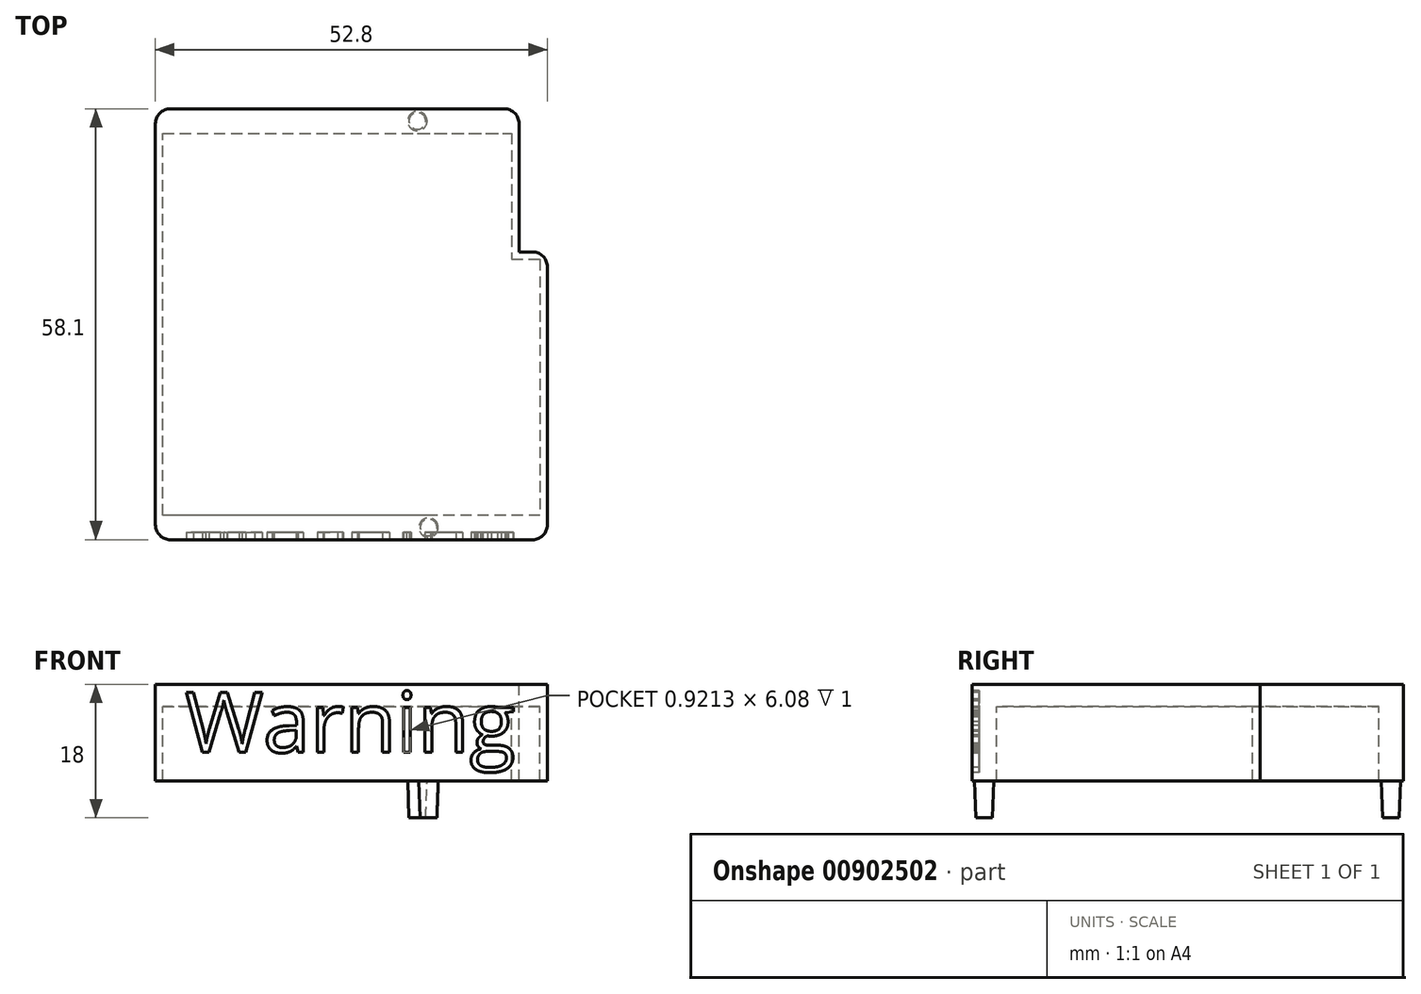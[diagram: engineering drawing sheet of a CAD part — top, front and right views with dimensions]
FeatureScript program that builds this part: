
annotation { "Feature Type Name" : "Feature", "Feature Type Description" : "" }
export const myFeature = defineFeature(function(context is Context, id is Id, definition is map)
    precondition{}
    {
        {
            var Q0;
            Q0=qCreatedBy(makeId("Top.planeOp"),FACE);
            var sketch = newSketch(context, id + "F0", { "sketchPlane" : qUnion([Q0])});
            skLineSegment(sketch, "E0", {"start": v(0, 0) * mm, "end": v(-50.8, 0) * mm});
            skLineSegment(sketch, "E1", {"start": v(-50.8, 0) * mm, "end": v(-50.8, 51.5) * mm});
            skLineSegment(sketch, "E2", {"start": v(-50.8, 51.5) * mm, "end": v(-3.81, 51.5) * mm});
            skLineSegment(sketch, "E3", {"start": v(-3.81, 51.5) * mm, "end": v(-3.81, 34.5) * mm});
            skLineSegment(sketch, "E4", {"start": v(-3.81, 34.5) * mm, "end": v(0, 34.5) * mm});
            skLineSegment(sketch, "E5", {"start": v(0, 34.5) * mm, "end": v(0, 0) * mm});
            skCircle(sketch, "E6", {"center": v(-15, -1.65) * mm, "radius": 1.65 * mm});
            skLineSegment(sketch, "E7", {"start": v(-49.8, -3.3) * mm, "end": v(-1, -3.3) * mm});
            skLineSegment(sketch, "E8", {"start": v(-51.8, -1.3) * mm, "end": v(-51.8, 52.8) * mm});
            skCircle(sketch, "E9", {"center": v(-16.51, 53.15) * mm, "radius": 1.65 * mm});
            skLineSegment(sketch, "E10", {"start": v(-49.8, 54.8) * mm, "end": v(-4.81, 54.8) * mm});
            skLineSegment(sketch, "E11", {"start": v(-2.81, 52.8) * mm, "end": v(-2.81, 35.5) * mm});
            skLineSegment(sketch, "E12", {"start": v(-2.81, 35.5) * mm, "end": v(-1, 35.5) * mm});
            skLineSegment(sketch, "E13", {"start": v(1, 33.5) * mm, "end": v(1, -1.3) * mm});
            skPoint(sketch, "E14.visualSharp", {"position": v(-51.8, -3.3) * mm});
            skArc(sketch, "E14.filletArc", {"start": v(-51.8, -1.3) * mm, "mid": v(-51.21, -2.71) * mm, "end": v(-49.8, -3.3) * mm});
            skPoint(sketch, "E15.visualSharp", {"position": v(-51.8, 54.8) * mm});
            skArc(sketch, "E15.filletArc", {"start": v(-49.8, 54.8) * mm, "mid": v(-51.21, 54.21) * mm, "end": v(-51.8, 52.8) * mm});
            skPoint(sketch, "E16.visualSharp", {"position": v(-2.81, 54.8) * mm});
            skArc(sketch, "E16.filletArc", {"start": v(-2.81, 52.8) * mm, "mid": v(-3.4, 54.21) * mm, "end": v(-4.81, 54.8) * mm});
            skPoint(sketch, "E17.visualSharp", {"position": v(1, -3.3) * mm});
            skArc(sketch, "E17.filletArc", {"start": v(-1, -3.3) * mm, "mid": v(0.41, -2.71) * mm, "end": v(1, -1.3) * mm});
            skPoint(sketch, "E18.visualSharp", {"position": v(1, 35.5) * mm});
            skArc(sketch, "E18.filletArc", {"start": v(1, 33.5) * mm, "mid": v(0.41, 34.91) * mm, "end": v(-1, 35.5) * mm});
            skSolve(sketch);
        }
        {
            var Q0;
            {var subQ13=sQuery(id+"F0.wireOp",EDGE,"E3");Q0=makeQuery(id+"F0.imprint","IMPRINT",FACE,{"disambiguationData":[TD([[makeQuery(id+"F0.imprint","IMPRINT",EDGE,{"derivedFrom":subQ13}),1.0]])]});}
            var Q1;
            {var subQ6=sQuery(id+"F0.wireOp",EDGE,"E1");Q1=makeQuery(id+"F0.imprint","IMPRINT",FACE,{"disambiguationData":[TD([[makeQuery(id+"F0.imprint","IMPRINT",EDGE,{"derivedFrom":subQ6}),1.0]])]});}
            var Q2;
            {var subQ0=sQuery(id+"F0.wireOp",EDGE,"E9");var subQ1=makeQuery(id+"F0.imprint","INTERSECT",VERTEX,{"derivedFrom":[subQ0,sQuery(id+"F0.wireOp",EDGE,"E10")]});Q2=makeQuery(id+"F0.imprint","IMPRINT",FACE,{"disambiguationData":[TD([[makeQuery(id+"F0.imprint","IMPRINT",EDGE,{"disambiguationData":[TD([[subQ1,-1.0]])],"derivedFrom":subQ0}),1.0]])]});}
            var Q3;
            {var subQ0=sQuery(id+"F0.wireOp",EDGE,"E6");var subQ1=makeQuery(id+"F0.imprint","INTERSECT",VERTEX,{"derivedFrom":[subQ0,sQuery(id+"F0.wireOp",EDGE,"E7")]});Q3=makeQuery(id+"F0.imprint","IMPRINT",FACE,{"disambiguationData":[TD([[makeQuery(id+"F0.imprint","IMPRINT",EDGE,{"disambiguationData":[TD([[subQ1,1.0]])],"derivedFrom":subQ0}),1.0]])]});}
            extrude(context, id + "F1", {"entities" : qUnion([Q0, Q1, Q2, Q3]), "oppositeDirection" : true, "depth" : 10 * mm, "offsetDistance" : 25 * mm});
        }
        {
            var Q0;
            Q0 = qSketchRegion(id + "F0", true);
            var Q1;
            {var subQ1=sQuery(id+"F0.wireOp",EDGE,"E1");Q1=makeQuery(id+"F0.imprint","IMPRINT",FACE,{"disambiguationData":[TD([[makeQuery(id+"F0.imprint","IMPRINT",EDGE,{"derivedFrom":subQ1}),-1.0]])]});}
            extrude(context, id + "F2", {"entities" : qUnion([Q0, Q1]), "operationType" : NewBodyOperationType.ADD, "depth" : 3 * mm, "offsetDistance" : 25 * mm});
        }
        {
            var Q0;
            {var subQ0=sQuery(id+"F0.wireOp",EDGE,"E6");var subQ1=makeQuery(id+"F0.imprint","INTERSECT",VERTEX,{"derivedFrom":[subQ0,sQuery(id+"F0.wireOp",EDGE,"E7")]});Q0=makeQuery(id+"F0.imprint","IMPRINT",FACE,{"disambiguationData":[TD([[makeQuery(id+"F0.imprint","IMPRINT",EDGE,{"disambiguationData":[TD([[subQ1,1.0]])],"derivedFrom":subQ0}),1.0]])]});}
            var Q1;
            {var subQ0=sQuery(id+"F0.wireOp",EDGE,"E9");var subQ1=makeQuery(id+"F0.imprint","INTERSECT",VERTEX,{"derivedFrom":[subQ0,sQuery(id+"F0.wireOp",EDGE,"E10")]});Q1=makeQuery(id+"F0.imprint","IMPRINT",FACE,{"disambiguationData":[TD([[makeQuery(id+"F0.imprint","IMPRINT",EDGE,{"disambiguationData":[TD([[subQ1,-1.0]])],"derivedFrom":subQ0}),1.0]])]});}
            extrude(context, id + "F3", {"entities" : qUnion([Q0, Q1]), "operationType" : NewBodyOperationType.ADD, "oppositeDirection" : true, "depth" : 15 * mm, "offsetDistance" : 25 * mm, "hasDraft" : true, "draftAngle" : 2 * degree, "draftPullDirection" : true});
        }
        {
            var Q0;
            {var subQ0=sQuery(id+"F0.wireOp",EDGE,"E7");Q0=makeQuery(id+"F2.boolean.opBoolean","MERGE",FACE,{"derivedFrom":[makeQuery(id+"F1.opExtrude","SWEPT_FACE",FACE,{"disambiguationData":[OSD([subQ0])]}),makeQuery(id+"F2.opExtrude","SWEPT_FACE",FACE,{"disambiguationData":[OSD([subQ0])]})]});}
            var sketch = newSketch(context, id + "F4", { "sketchPlane" : qUnion([Q0])});
            skText(sketch, "E19", { "text": "Warning", "fontName": "OpenSans-Regular.ttf"});
            const initialGuessF4  = {"E19": [-0.0478, -0.00618, 1, 0, 0.00818]};
            skSetInitialGuess(sketch, initialGuessF4);
            skSolve(sketch);
        }
        {
            var Q0;
            Q0 = qSketchRegion(id + "F4", true);
            extrude(context, id + "F5", {"entities" : qUnion([Q0]), "operationType" : NewBodyOperationType.REMOVE, "oppositeDirection" : true, "depth" : 1 * mm, "offsetDistance" : 25 * mm});
        }
    });
